MODEL slx_599ce87c5c5d
CONFIG AbsTol = auto
CONFIG EnableMultiTasking = off
CONFIG FixedStep = 0.01
CONFIG MaxStep = auto
CONFIG MinStep = auto
CONFIG RelTol = 1e-3
CONFIG SampleTimeConstraint = Unconstrained
CONFIG Solver = ode4
CONFIG SolverName = ode4
CONFIG StartTime = 0.0
CONFIG StopTime = 10.0
BLOCK [Sum] Add
  InputSameDT = off
  Inputs = +++
  OutDataTypeStr = Inherit: Inherit via internal rule
  Ports = [3, 1]
  SaturateOnIntegerOverflow = off
BLOCK [Gain] Gain
  Gain = -0.5
  OutDataTypeStr = Inherit: Inherit via internal rule
  ParamDataTypeStr = Inherit: Inherit via internal rule
  SaturateOnIntegerOverflow = off
BLOCK [Gain] Gain1
  Gain = -2
  OutDataTypeStr = Inherit: Inherit via internal rule
  ParamDataTypeStr = Inherit: Inherit via internal rule
  SaturateOnIntegerOverflow = off
BLOCK [Gain] Gain2
  Gain = -3
  OutDataTypeStr = Inherit: Inherit via internal rule
  ParamDataTypeStr = Inherit: Inherit via internal rule
  SaturateOnIntegerOverflow = off
BLOCK [Integrator] Integrator
  InitialCondition = 1
  Ports = [1, 1]
BLOCK [Integrator] Integrator1
  InitialCondition = 1
  Ports = [1, 1]
BLOCK [Product] Product
  InputSameDT = off
  Inputs = 3
  OutDataTypeStr = Inherit: Inherit via internal rule
  Ports = [3, 1]
  RndMeth = Floor
  SaturateOnIntegerOverflow = off
BLOCK [Scope] Scope
  Floating = off
  NumInputPorts = 1
  Ports = [1]
  ScopeSpecificationString = Simulink.scopes.TimeScopeBlockCfg('CurrentConfiguration', extmgr.ConfigurationSet(extmgr.Configuration('Core','General UI',true),extmgr.Configuration('Core','Source UI',true),extmgr.Configuration('Sources','WiredSimulink',true),extmgr.Configuration('Visuals','Time Domain',true,'SerializedDisplays',{struct('MinYLimReal','-7.2134','MaxYLimReal','4.20473','YLabelReal','','MinYLimMag','0.00000','MaxYL...<+1345ch>
BLOCK [Scope] Scope1
  Floating = off
  NumInputPorts = 1
  Ports = [1]
  ScopeSpecificationString = Simulink.scopes.TimeScopeBlockCfg('CurrentConfiguration', extmgr.ConfigurationSet(extmgr.Configuration('Core','General UI',true),extmgr.Configuration('Core','Source UI',true),extmgr.Configuration('Sources','WiredSimulink',true,'DataLoggingVariableName','ScopeData1'),extmgr.Configuration('Visuals','Time Domain',true,'SerializedDisplays',{struct('MinYLimReal','-7.2134','MaxYLimReal','4.20473','YLabe...<+1384ch>
LINE Add:1 -> Integrator:1
LINE Add:1 -> Scope:1
LINE Gain1:1 -> Add:2
LINE Gain2:1 -> Add:3
LINE Gain:1 -> Add:1
LINE Integrator1:1 -> Gain1:1
LINE Integrator1:1 -> Product:1
LINE Integrator1:1 -> Product:2
LINE Integrator1:1 -> Product:3
LINE Integrator:1 -> Gain:1
LINE Integrator:1 -> Integrator1:1
LINE Integrator:1 -> Scope1:1
LINE Product:1 -> Gain2:1
